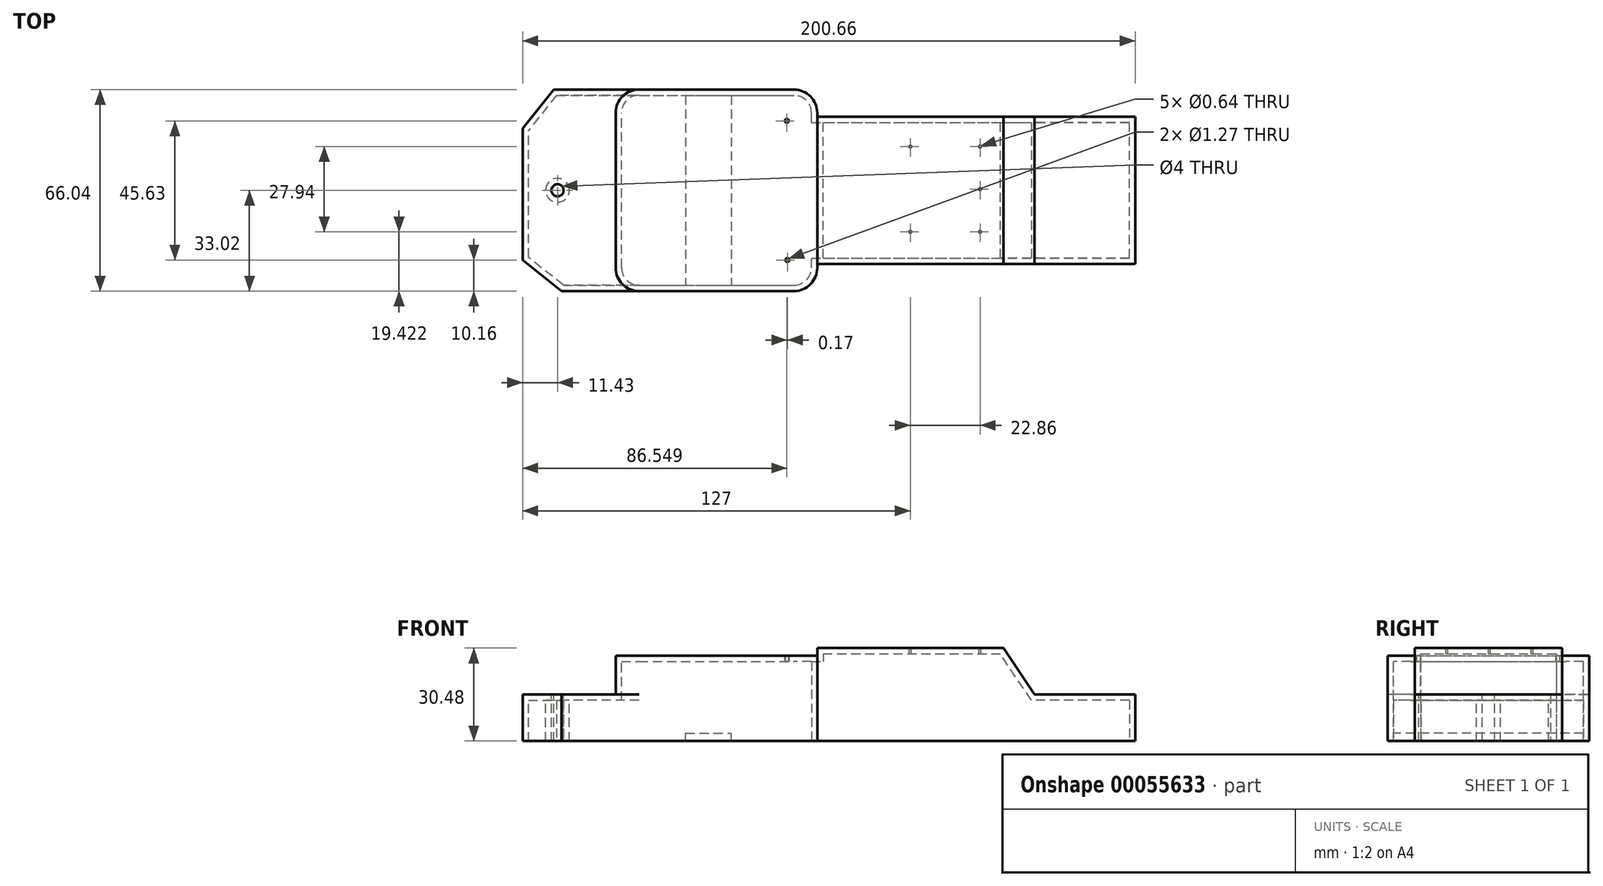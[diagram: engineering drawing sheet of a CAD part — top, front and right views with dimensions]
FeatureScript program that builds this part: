
annotation { "Feature Type Name" : "Feature", "Feature Type Description" : "" }
export const myFeature = defineFeature(function(context is Context, id is Id, definition is map)
    precondition{}
    {
        {
            var Q0;
            Q0=qCreatedBy(makeId("Top.planeOp"),FACE);
            var sketch = newSketch(context, id + "F0", { "sketchPlane" : qUnion([Q0])});
            skLineSegment(sketch, "E0.bottom", {"start": v(0, 0) * mm, "end": v(66.04, 0) * mm});
            skLineSegment(sketch, "E0.top", {"start": v(0, 66.04) * mm, "end": v(66.04, 66.04) * mm});
            skLineSegment(sketch, "E0.left", {"start": v(0, 0) * mm, "end": v(0, 66.04) * mm});
            skLineSegment(sketch, "E0.right", {"start": v(66.04, 0) * mm, "end": v(66.04, 66.04) * mm});
            skLineSegment(sketch, "E1.bottom", {"start": v(0, 0) * mm, "end": v(-30.48, 0) * mm});
            skLineSegment(sketch, "E1.top", {"start": v(0, 66.04) * mm, "end": v(-30.48, 66.04) * mm});
            skLineSegment(sketch, "E1.right", {"start": v(-30.48, 0) * mm, "end": v(-30.48, 66.04) * mm});
            skLineSegment(sketch, "E2", {"start": v(43.13, 0) * mm, "end": v(66.04, 0) * mm, "construction": true});
            skLineSegment(sketch, "E3", {"start": v(43.13, 66.04) * mm, "end": v(66.04, 66.04) * mm, "construction": true});
            skSolve(sketch);
        }
        {
            var Q0;
            Q0=makeQuery(id+"F0.imprint","IMPRINT",FACE,{"disambiguationData":[TD([[makeQuery(id+"F0.imprint","IMPRINT",EDGE,{"derivedFrom":sQuery(id+"F0.wireOp",EDGE,"E0.bottom")}),1.0]])]});
            extrude(context, id + "F1", {"entities" : qUnion([Q0]), "depth" : 27.94 * mm});
        }
        {
            var Q0;
            Q0=qCreatedBy(makeId("Top.planeOp"),FACE);
            var sketch = newSketch(context, id + "F2", { "sketchPlane" : qUnion([Q0])});
            skLineSegment(sketch, "E4.bottom", {"start": v(0, 0) * mm, "end": v(-30.48, 0) * mm});
            skLineSegment(sketch, "E4.top", {"start": v(0, 66.04) * mm, "end": v(-30.48, 66.04) * mm});
            skLineSegment(sketch, "E4.left", {"start": v(0, 0) * mm, "end": v(0, 66.04) * mm});
            skLineSegment(sketch, "E4.right", {"start": v(-30.48, 0) * mm, "end": v(-30.48, 66.04) * mm});
            skSolve(sketch);
        }
        {
            var Q0;
            Q0=makeQuery(id+"F2.imprint","IMPRINT",FACE,{"disambiguationData":[TD([[makeQuery(id+"F2.imprint","IMPRINT",EDGE,{"derivedFrom":sQuery(id+"F2.wireOp",EDGE,"E4.bottom")}),-1.0]])]});
            extrude(context, id + "F3", {"entities" : qUnion([Q0]), "operationType" : NewBodyOperationType.ADD, "depth" : 15.24 * mm});
        }
        {
            var Q0;
            Q0=qCreatedBy(makeId("Top.planeOp"),FACE);
            var sketch = newSketch(context, id + "F4", { "sketchPlane" : qUnion([Q0])});
            skLineSegment(sketch, "E5.bottom", {"start": v(66.04, 8.89) * mm, "end": v(137.16, 8.9) * mm});
            skLineSegment(sketch, "E5.top", {"start": v(66.04, 57.15) * mm, "end": v(137.16, 57.15) * mm});
            skLineSegment(sketch, "E5.left", {"start": v(66.04, 8.89) * mm, "end": v(66.04, 57.15) * mm});
            skLineSegment(sketch, "E5.right", {"start": v(137.16, 8.9) * mm, "end": v(137.16, 57.15) * mm});
            skSolve(sketch);
        }
        {
            var Q0;
            Q0=qSketchRegion(id+"F4",true);
            var Q1;
            Q1=makeQuery(id+"F4.imprint","IMPRINT",FACE,{"disambiguationData":[TD([[makeQuery(id+"F4.imprint","IMPRINT",EDGE,{"derivedFrom":sQuery(id+"F4.wireOp",EDGE,"E5.bottom")}),1.0]])]});
            extrude(context, id + "F5", {"entities" : qUnion([Q0, Q1]), "operationType" : NewBodyOperationType.ADD, "depth" : 30.48 * mm});
        }
        {
            var Q0;
            Q0=makeQuery(id+"F3.opExtrude","SWEPT_EDGE",EDGE,{"disambiguationData":[OSD([sQuery(id+"F2.wireOp",EDGE,"E4.bottom"),sQuery(id+"F2.wireOp",EDGE,"E4.right")])]});
            chamfer(context, id + "F6", {"entities" : qUnion([Q0]), "chamferType" : ChamferType.TWO_OFFSETS, "width1" : 12.7 * mm, "oppositeDirection" : false, "width2" : 10.16 * mm, "tangentPropagation" : true});
        }
        {
            var Q0;
            Q0=makeQuery(id+"F3.opExtrude","SWEPT_EDGE",EDGE,{"disambiguationData":[OSD([sQuery(id+"F2.wireOp",EDGE,"E4.top"),sQuery(id+"F2.wireOp",EDGE,"E4.right")])]});
            chamfer(context, id + "F7", {"entities" : qUnion([Q0]), "chamferType" : ChamferType.TWO_OFFSETS, "width1" : 12.7 * mm, "oppositeDirection" : false, "width2" : 10.16 * mm, "tangentPropagation" : true});
        }
        {
            var Q0;
            Q0=makeQuery(id+"F1.opExtrude","SWEPT_EDGE",EDGE,{"disambiguationData":[OSD([sQuery(id+"F0.wireOp",EDGE,"E0.bottom"),sQuery(id+"F0.wireOp",EDGE,"E1.bottom"),sQuery(id+"F0.wireOp",EDGE,"E0.left")])]});
            var Q1;
            Q1=makeQuery(id+"F1.opExtrude","SWEPT_EDGE",EDGE,{"disambiguationData":[OSD([sQuery(id+"F0.wireOp",EDGE,"E0.top"),sQuery(id+"F0.wireOp",EDGE,"E1.top"),sQuery(id+"F0.wireOp",EDGE,"E0.left")])]});
            fillet(context, id + "F8", {"entities" : qUnion([Q0, Q1]), "radius" : 7.62 * mm, "tangentPropagation" : true, "allowEdgeOverflow" : false});
        }
        {
            var Q0;
            Q0=makeQuery(id+"F1.opExtrude","SWEPT_EDGE",EDGE,{"disambiguationData":[OSD([sQuery(id+"F0.wireOp",EDGE,"E0.top"),sQuery(id+"F0.wireOp",EDGE,"E0.right")])]});
            var Q1;
            Q1=makeQuery(id+"F1.opExtrude","SWEPT_EDGE",EDGE,{"disambiguationData":[OSD([sQuery(id+"F0.wireOp",EDGE,"E0.bottom"),sQuery(id+"F0.wireOp",EDGE,"E0.right")])]});
            fillet(context, id + "F9", {"entities" : qUnion([Q0, Q1]), "radius" : 7.62 * mm, "tangentPropagation" : true, "allowEdgeOverflow" : false});
        }
        {
            var Q0;
            Q0=makeQuery(id+"F5.opExtrude","CAP_EDGE",EDGE,{"disambiguationData":[OSD([sQuery(id+"F4.wireOp",EDGE,"E5.right")])],"isStart":false});
            chamfer(context, id + "F10", {"entities" : qUnion([Q0]), "chamferType" : ChamferType.TWO_OFFSETS, "width1" : 10.16 * mm, "oppositeDirection" : false, "width2" : 15.24 * mm, "tangentPropagation" : true});
        }
        {
            var Q0;
            Q0=makeQuery(id+"F5.opExtrude","SWEPT_FACE",FACE,{"disambiguationData":[OSD([sQuery(id+"F4.wireOp",EDGE,"E5.right")])]});
            extrude(context, id + "F11", {"entities" : qUnion([Q0]), "operationType" : NewBodyOperationType.ADD, "depth" : 33.02 * mm});
        }
        {
            var Q0;
            Q0=makeQuery(id+"F3.opExtrude","CAP_FACE",FACE,{"disambiguationData":[OSD([sQuery(id+"F2.wireOp",EDGE,"E4.bottom"),sQuery(id+"F2.wireOp",EDGE,"E4.top"),sQuery(id+"F2.wireOp",EDGE,"E4.left"),sQuery(id+"F2.wireOp",EDGE,"E4.right")])],"isStart":false});
            var sketch = newSketch(context, id + "F12", { "sketchPlane" : qUnion([Q0])});
            skCircle(sketch, "E6", {"center": v(-19.05, 33.02) * mm, "radius": 2.07 * mm});
            skSolve(sketch);
        }
        {
            var Q0;
            Q0=sQuery(id+"F12.wireOp",VERTEX,"E6.center");
            var Q1;
            Q1=makeQuery(id+"F1.opExtrude","SWEPT_BODY",BODY,{"disambiguationData":[OSD([sQuery(id+"F0.wireOp",EDGE,"E0.bottom"),sQuery(id+"F0.wireOp",EDGE,"E0.top"),sQuery(id+"F0.wireOp",EDGE,"E0.right"),sQuery(id+"F0.wireOp",EDGE,"E0.left")])]});
            hole(context, id + "F13", {"style" : HoleStyle.SIMPLE, "holeDiameter" : 4 * mm, "endStyle" : HoleEndStyle.THROUGH, "locations" : qUnion([Q0]), "scope" : qUnion([Q1])});
        }
        {
            var Q0;
            {var subQ0=sQuery(id+"F4.wireOp",EDGE,"E5.right");Q0=makeQuery(id+"F11.boolean.opBoolean","MERGE",FACE,{"derivedFrom":[makeQuery(id+"F5.boolean.opBoolean","MERGE",FACE,{"derivedFrom":[makeQuery(id+"F3.boolean.opBoolean","MERGE",FACE,{"derivedFrom":[makeQuery(id+"F1.opExtrude","CAP_FACE",FACE,{"disambiguationData":[OSD([sQuery(id+"F0.wireOp",EDGE,"E0.bottom"),sQuery(id+"F0.wireOp",EDGE,"E0.top"),sQuery(id+"F0.wireOp",EDGE,"E0.right"),sQuery(id+"F0.wireOp",EDGE,"E0.left")])],"isStart":true}),makeQuery(id+"F3.opExtrude","CAP_FACE",FACE,{"disambiguationData":[OSD([sQuery(id+"F2.wireOp",EDGE,"E4.bottom"),sQuery(id+"F2.wireOp",EDGE,"E4.top"),sQuery(id+"F2.wireOp",EDGE,"E4.left"),sQuery(id+"F2.wireOp",EDGE,"E4.right")])],"isStart":true})]}),makeQuery(id+"F5.opExtrude","CAP_FACE",FACE,{"disambiguationData":[OSD([sQuery(id+"F4.wireOp",EDGE,"E5.bottom"),sQuery(id+"F4.wireOp",EDGE,"E5.top"),sQuery(id+"F4.wireOp",EDGE,"E5.left"),subQ0])],"isStart":true})]}),makeQuery(id+"F11.opExtrude","SWEPT_FACE",FACE,{"disambiguationData":[OSD([subQ0]),TDD([makeQuery(id+"F5.opExtrude","CAP_EDGE",EDGE,{"disambiguationData":[OSD([subQ0])],"isStart":true})])]})]});}
            shell(context, id + "F14", {"entities" : qUnion([Q0]), "thickness" : 1.9 * mm});
        }
        {
            var Q0;
            Q0=makeQuery(id+"F1.opExtrude","CAP_FACE",FACE,{"disambiguationData":[OSD([sQuery(id+"F0.wireOp",EDGE,"E0.bottom"),sQuery(id+"F0.wireOp",EDGE,"E0.top"),sQuery(id+"F0.wireOp",EDGE,"E0.right"),sQuery(id+"F0.wireOp",EDGE,"E0.left")])],"isStart":false});
            var sketch = newSketch(context, id + "F15", { "sketchPlane" : qUnion([Q0])});
            skLineSegment(sketch, "E7.bottom", {"start": v(66.23, 65.95) * mm, "end": v(56.07, 65.95) * mm});
            skLineSegment(sketch, "E7.top", {"start": v(66.23, 55.8) * mm, "end": v(56.07, 55.8) * mm});
            skLineSegment(sketch, "E7.left", {"start": v(66.23, 65.95) * mm, "end": v(66.23, 55.8) * mm});
            skLineSegment(sketch, "E7.right", {"start": v(56.07, 65.95) * mm, "end": v(56.07, 55.8) * mm});
            skLineSegment(sketch, "E8.bottom", {"start": v(66.4, 0) * mm, "end": v(56.24, 0) * mm});
            skLineSegment(sketch, "E8.top", {"start": v(66.4, 10.16) * mm, "end": v(56.24, 10.16) * mm});
            skLineSegment(sketch, "E8.left", {"start": v(66.4, 0) * mm, "end": v(66.4, 10.16) * mm});
            skLineSegment(sketch, "E8.right", {"start": v(56.24, 0) * mm, "end": v(56.24, 10.16) * mm});
            skSolve(sketch);
        }
        {
            var Q0;
            Q0=sQuery(id+"F15.wireOp",VERTEX,"E8.top.end");
            var Q1;
            Q1=sQuery(id+"F15.wireOp",VERTEX,"E7.right.end");
            var Q2;
            Q2=makeQuery(id+"F1.opExtrude","SWEPT_BODY",BODY,{"disambiguationData":[OSD([sQuery(id+"F0.wireOp",EDGE,"E0.bottom"),sQuery(id+"F0.wireOp",EDGE,"E0.top"),sQuery(id+"F0.wireOp",EDGE,"E0.right"),sQuery(id+"F0.wireOp",EDGE,"E0.left")])]});
            hole(context, id + "F16", {"style" : HoleStyle.SIMPLE, "holeDiameter" : 1.27 * mm, "endStyle" : HoleEndStyle.THROUGH, "locations" : qUnion([Q0, Q1]), "scope" : qUnion([Q2])});
        }
        {
            var Q0;
            Q0=makeQuery(id+"F5.opExtrude","CAP_FACE",FACE,{"disambiguationData":[OSD([sQuery(id+"F4.wireOp",EDGE,"E5.bottom"),sQuery(id+"F4.wireOp",EDGE,"E5.top"),sQuery(id+"F4.wireOp",EDGE,"E5.left"),sQuery(id+"F4.wireOp",EDGE,"E5.right")])],"isStart":false});
            var sketch = newSketch(context, id + "F17", { "sketchPlane" : qUnion([Q0])});
            skLineSegment(sketch, "E9.bottom", {"start": v(96.52, 33.4) * mm, "end": v(119.38, 33.4) * mm});
            skLineSegment(sketch, "E9.top", {"start": v(96.52, 19.42) * mm, "end": v(119.38, 19.42) * mm});
            skLineSegment(sketch, "E9.left", {"start": v(96.52, 33.4) * mm, "end": v(96.52, 19.42) * mm});
            skLineSegment(sketch, "E9.right", {"start": v(119.38, 33.4) * mm, "end": v(119.38, 19.42) * mm});
            skLineSegment(sketch, "E10.MirrorCS", {"start": v(96.52, 33.4) * mm, "end": v(96.52, 47.36) * mm});
            skLineSegment(sketch, "E11.MirrorCS", {"start": v(119.38, 33.4) * mm, "end": v(119.38, 47.36) * mm});
            skLineSegment(sketch, "E12.MirrorCS", {"start": v(96.52, 47.36) * mm, "end": v(119.38, 47.36) * mm});
            skSolve(sketch);
        }
        {
            var Q0;
            Q0=sQuery(id+"F17.wireOp",VERTEX,"E12.MirrorCS.start");
            var Q1;
            Q1=sQuery(id+"F17.wireOp",VERTEX,"E11.MirrorCS.end");
            var Q2;
            Q2=sQuery(id+"F17.wireOp",VERTEX,"E9.right.start");
            var Q3;
            Q3=sQuery(id+"F17.wireOp",VERTEX,"E9.right.end");
            var Q4;
            Q4=sQuery(id+"F17.wireOp",VERTEX,"E9.left.end");
            var Q5;
            Q5=makeQuery(id+"F1.opExtrude","SWEPT_BODY",BODY,{"disambiguationData":[OSD([sQuery(id+"F0.wireOp",EDGE,"E0.bottom"),sQuery(id+"F0.wireOp",EDGE,"E0.top"),sQuery(id+"F0.wireOp",EDGE,"E0.right"),sQuery(id+"F0.wireOp",EDGE,"E0.left")])]});
            hole(context, id + "F18", {"style" : HoleStyle.SIMPLE, "holeDiameter" : 0.64 * mm, "endStyle" : HoleEndStyle.THROUGH, "locations" : qUnion([Q0, Q1, Q2, Q3, Q4]), "scope" : qUnion([Q5])});
        }
        {
            var Q0;
            Q0=makeQuery(id+"F14.opShell","OFFSET_FACE",FACE,{"disambiguationData":[OSD([sQuery(id+"F0.wireOp",EDGE,"E0.bottom"),sQuery(id+"F2.wireOp",EDGE,"E4.bottom")])]});
            var sketch = newSketch(context, id + "F19", { "sketchPlane" : qUnion([Q0])});
            skLineSegment(sketch, "E13.bottom", {"start": v(-22.89, 0) * mm, "end": v(-37.89, 0) * mm});
            skLineSegment(sketch, "E13.top", {"start": v(-22.89, 2.5) * mm, "end": v(-37.89, 2.5) * mm});
            skLineSegment(sketch, "E13.left", {"start": v(-22.89, 0) * mm, "end": v(-22.89, 2.5) * mm});
            skLineSegment(sketch, "E13.right", {"start": v(-37.89, 0) * mm, "end": v(-37.89, 2.5) * mm});
            skLineSegment(sketch, "E14", {"start": v(-22.89, 0) * mm, "end": v(17.11, 0) * mm, "construction": true});
            skLineSegment(sketch, "E15", {"start": v(17.11, 0) * mm, "end": v(-22.89, 0) * mm, "construction": true});
            skSolve(sketch);
        }
        {
            var Q0;
            Q0=makeQuery(id+"F19.imprint","IMPRINT",FACE,{"disambiguationData":[TD([[makeQuery(id+"F19.imprint","IMPRINT",EDGE,{"derivedFrom":sQuery(id+"F19.wireOp",EDGE,"E13.bottom")}),-1.0]])]});
            var Q1;
            {var subQ0=sQuery(id+"F4.wireOp",EDGE,"E5.right");Q1=makeQuery(id+"F11.boolean.opBoolean","MERGE",FACE,{"derivedFrom":[makeQuery(id+"F5.boolean.opBoolean","MERGE",FACE,{"derivedFrom":[makeQuery(id+"F3.boolean.opBoolean","MERGE",FACE,{"derivedFrom":[makeQuery(id+"F1.opExtrude","CAP_FACE",FACE,{"disambiguationData":[OSD([sQuery(id+"F0.wireOp",EDGE,"E0.bottom"),sQuery(id+"F0.wireOp",EDGE,"E0.top"),sQuery(id+"F0.wireOp",EDGE,"E0.right"),sQuery(id+"F0.wireOp",EDGE,"E0.left")])],"isStart":true}),makeQuery(id+"F3.opExtrude","CAP_FACE",FACE,{"disambiguationData":[OSD([sQuery(id+"F2.wireOp",EDGE,"E4.bottom"),sQuery(id+"F2.wireOp",EDGE,"E4.top"),sQuery(id+"F2.wireOp",EDGE,"E4.left"),sQuery(id+"F2.wireOp",EDGE,"E4.right")])],"isStart":true})]}),makeQuery(id+"F5.opExtrude","CAP_FACE",FACE,{"disambiguationData":[OSD([sQuery(id+"F4.wireOp",EDGE,"E5.bottom"),sQuery(id+"F4.wireOp",EDGE,"E5.top"),sQuery(id+"F4.wireOp",EDGE,"E5.left"),subQ0])],"isStart":true})]}),makeQuery(id+"F11.opExtrude","SWEPT_FACE",FACE,{"disambiguationData":[OSD([subQ0]),TDD([makeQuery(id+"F5.opExtrude","CAP_EDGE",EDGE,{"disambiguationData":[OSD([subQ0])],"isStart":true})])]})]});}
            extrude(context, id + "F20", {"entities" : qUnion([Q0]), "operationType" : NewBodyOperationType.ADD, "endBound" : BoundingType.UP_TO_NEXT, "endBoundEntityFace" : qUnion([Q1]), "depth" : 10 * mm});
        }
    });
